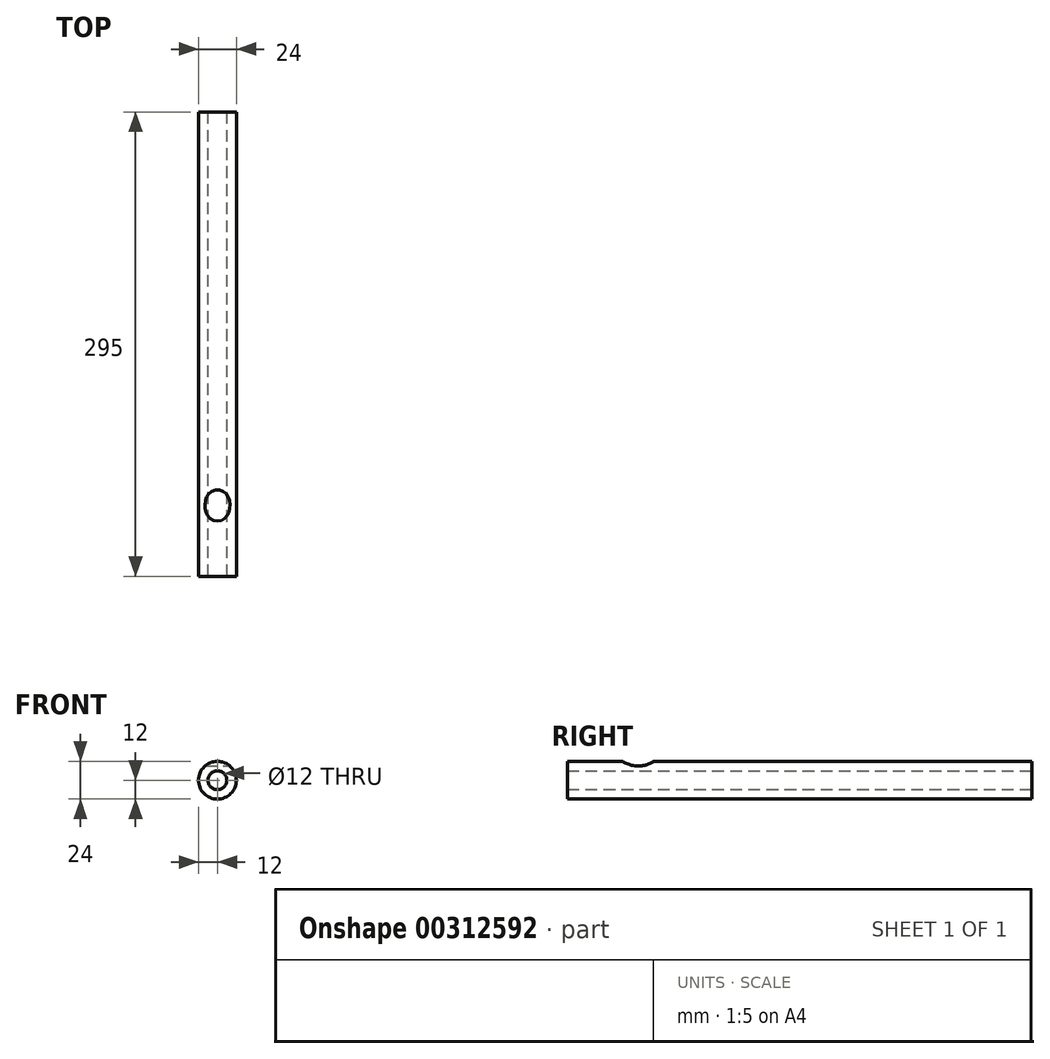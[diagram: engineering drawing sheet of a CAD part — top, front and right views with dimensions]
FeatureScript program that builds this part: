
annotation { "Feature Type Name" : "Feature", "Feature Type Description" : "" }
export const myFeature = defineFeature(function(context is Context, id is Id, definition is map)
    precondition{}
    {
        {
            var Q0;
            Q0=qCreatedBy(makeId("Front.planeOp"),FACE);
            var sketch = newSketch(context, id + "F0", { "sketchPlane" : qUnion([Q0])});
            skCircle(sketch, "E0", {"center": v(0, 0) * mm, "radius": 6 * mm});
            skCircle(sketch, "E1", {"center": v(0, 0) * mm, "radius": 12 * mm});
            skSolve(sketch);
        }
        {
            var Q0;
            Q0 = qSketchRegion(id + "F0", true);
            extrude(context, id + "F1", {"entities" : qUnion([Q0]), "depth" : 295 * mm});
        }
        {
            var Q0;
            Q0=makeQuery(id+"F1.opExtrude","CAP_FACE",FACE,{"disambiguationData":[OSD([sQuery(id+"F0.wireOp",EDGE,"E0"),sQuery(id+"F0.wireOp",EDGE,"E1")])],"isStart":false});
            var sketch = newSketch(context, id + "F2", { "sketchPlane" : qUnion([Q0])});
            skCircle(sketch, "E2", {"center": v(0, 0) * mm, "radius": 12 * mm});
            skSolve(sketch);
        }
        {
            var Q0;
            Q0=qCreatedBy(makeId("Right.planeOp"),FACE);
            var sketch = newSketch(context, id + "F3", { "sketchPlane" : qUnion([Q0])});
            skLineSegment(sketch, "E3.0", {"start": v(-295, -12) * mm, "end": v(-295, 12) * mm});
            skCircle(sketch, "E4", {"center": v(-250, 26.5) * mm, "radius": 17.5 * mm});
            skSolve(sketch);
        }
        {
            var Q0;
            Q0=makeQuery(id+"F3.imprint","IMPRINT",FACE,{"disambiguationData":[TD([[makeQuery(id+"F3.imprint","IMPRINT",EDGE,{"derivedFrom":sQuery(id+"F3.wireOp",EDGE,"E4")}),1.0]])]});
            extrude(context, id + "F4", {"entities" : qUnion([Q0]), "operationType" : NewBodyOperationType.REMOVE, "endBound" : BoundingType.SYMMETRIC, "oppositeDirection" : true, "depth" : 25 * mm});
        }
    });
